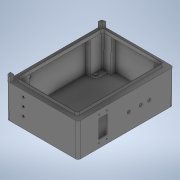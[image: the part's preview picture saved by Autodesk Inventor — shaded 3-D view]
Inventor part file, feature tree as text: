
AUTODESK INVENTOR PART (.ipt)
format: ipt  version: 2021 (Build 250183000, 183)  size: 601,088 bytes
history: native  units: mm
features: extrude x18, sketch x17, projected_geometry x17, draft x7, plane x6, hole x3, fillet x2, shell x1
ambient origin geometry x8: Origin, YZ Plane, XZ Plane, XY Plane, X Axis, Y Axis, Z Axis, Center Point
bodies: Solid1 (feature_tree)
feature tree (71):
  extrude  "Extrusion1"  Depth=398.5mm
  extrude  "Extrusion2"  Depth=139.8mm
  shell  "Shell1"  Thickness=256.0mm
  extrude  "Extrusion3"  Depth=10.0mm
  plane  "Work Plane1"
  plane  "Work Plane2"
  plane  "Work Plane3"
  plane  "Work Plane4"
  plane  "Work Plane5"
  plane  "Work Plane6"
  sketch  "Sketch4"  dims[d8=11.8mm d9=0.0mm d10=2.7mm]
  extrude  "Extrusion4"  Depth=2.7mm
  extrude  "Extrusion5"  Depth=17.0mm TaperAngle=0.0deg
  sketch  "Sketch5"  dims[d11=2.4mm d12=17.0mm d13=0.0mm]
  extrude  "Extrusion6"  Depth=247.0mm
  extrude  "Extrusion7"  Depth=14.0mm TaperAngle=0.0deg
  extrude  "Extrusion8"  Depth=14.0mm TaperAngle=0.0deg
  extrude  "Extrusion9"  Depth=351.5mm
  draft  "FaceDraft1"
  draft  "FaceDraft2"
  draft  "FaceDraft3"
  draft  "FaceDraft4"
  draft  "FaceDraft5"
  draft  "FaceDraft6"
  draft  "FaceDraft7"
  fillet  "Fillet1"  Radius=14.0mm
  extrude  "Extrusion10"  Depth=14.0mm
  extrude  "Extrusion11"  Depth=0.174533mm
  extrude  "Extrusion12"  Depth=0.174533mm
  extrude  "Extrusion13"  Depth=0.174533mm
  sketch  "Sketch13"  dims[d34=0.174533mm d35=0.174533mm]
  extrude  "Extrusion15"  Depth=20.0mm
  hole  "Hole2"  [1 undecoded]
  extrude  "Extrusion16"  Depth=15.82mm
  fillet  "Fillet2"  Radius=15.82mm
  hole  "Hole3"  [1 undecoded]
  extrude  "Extrusion17"  Depth=6.0mm
  extrude  "Extrusion18"  Depth=6.0mm
  extrude  "Extrusion20"  Depth=6.0mm
  hole  "Hole4"  [1 undecoded]
  sketch  "Sketch1"  dims[d0=298.5mm d1=398.5mm]
  sketch  "Sketch2"  dims[d2=10.0mm d3=139.8mm d4=0.053646mm d5=256.0mm]
  sketch  "Sketch3"  dims[d6=361.5mm d7=10.0mm]
  projected_geometry  "Projected Loop1"
  sketch  "Sketch6"  dims[d14=126.8mm d15=-126.8mm d16=89.5mm d17=-89.5mm d18=247.0mm]
  projected_geometry  "Projected Loop2"
  projected_geometry  "Projected Loop3"
  sketch  "Sketch7"  dims[d19=14.0mm d20=0.0mm d21=14.0mm d22=0.0mm]
  projected_geometry  "Projected Loop4"
  projected_geometry  "Projected Loop5"
  sketch  "Sketch8"  dims[d23=247.0mm d24=14.0mm d25=0.0mm]
  projected_geometry  "Projected Loop6"
  sketch  "Sketch9"  dims[d26=14.0mm d27=0.0mm d28=351.5mm d29=14.0mm d30=0.0mm]
  projected_geometry  "Projected Loop7"
  projected_geometry  "Projected Loop8"
  projected_geometry  "Projected Loop9"
  projected_geometry  "Projected Loop10"
  sketch  "Sketch11"  dims[d31=14.0mm d32=0.0mm d33=0.174533mm]
  sketch  "Sketch14"  dims[d36=0.174533mm d37=0.174533mm]
  projected_geometry  "Projected Loop11"
  sketch  "Sketch15"  dims[d38=0.174533mm d39=0.174533mm]
  sketch  "Sketch16"  dims[d40=6.0mm d41=20.0mm]
  projected_geometry  "Projected Loop12"
  sketch  "Sketch17"  dims[d43=12.0mm d44=8.2mm d45=0.0mm]
  projected_geometry  "Projected Loop13"
  sketch  "Sketch19"  dims[d46=15.82mm d47=15.82mm d48=15.82mm]
  projected_geometry  "Projected Loop14"
  projected_geometry  "Projected Loop15"
  projected_geometry  "Projected Loop16"
  projected_geometry  "Projected Loop17"
  sketch  "Sketch20"  dims[d49=15.82mm d50=227.778mm d51=227.778mm d52=275.67mm d53=275.67mm d54=113.889mm d55=113.889mm d56=137.835mm d57=137.835mm d58=8.0mm d59=0.0mm d60=7.9mm d61=7.9mm d62=7.9mm d63=7.9mm d64=7.9mm d65=0.0mm d66=245.0mm d67=289.0mm d68=211.0mm d69=259.0mm d70=2.0mm d71=0.0mm d86=32.0mm d87=103.0mm d88=70.0mm d89=85.0mm d90=35.0mm d91=76.0mm d92=10.0mm d93=0.0mm d94=4.5mm d95=6.0mm d96=9.4mm d97=2.0mm d98=90.0deg d99=8.0mm d100=20.594885mm d101=2.0mm d102=15.8mm d103=15.4mm d104=23.0mm d105=0.0mm d106=2.0mm d107=90.0mm d108=175.0mm d109=140.0mm d110=12.2mm d111=6.0mm d112=4.0mm d113=2.0mm d114=90.0deg d115=8.0mm d116=20.594885mm d117=20.0mm d118=45.0mm d119=22.0mm d127=23.0mm d128=0.0mm d129=12.0mm d130=60.0mm d131=8.2mm d132=8.2mm d133=45.0mm d134=70.0mm d135=35.0mm d136=60.0mm d137=8.2mm d138=23.0mm d139=0.0mm d148=8.2mm d149=8.2mm d150=8.2mm d151=8.2mm d152=0.0mm d153=0.0mm d154=213.0mm d155=335.0mm d156=3.0mm d157=6.0mm d158=4.0mm d159=2.0mm d160=90.0deg d161=6.0mm d162=20.594885mm]
note: 3 required parameter values undecoded (feature->parameter linkage not recoverable at this tier; creation-order binding heuristic only, values carry confidence <= 0.55)
